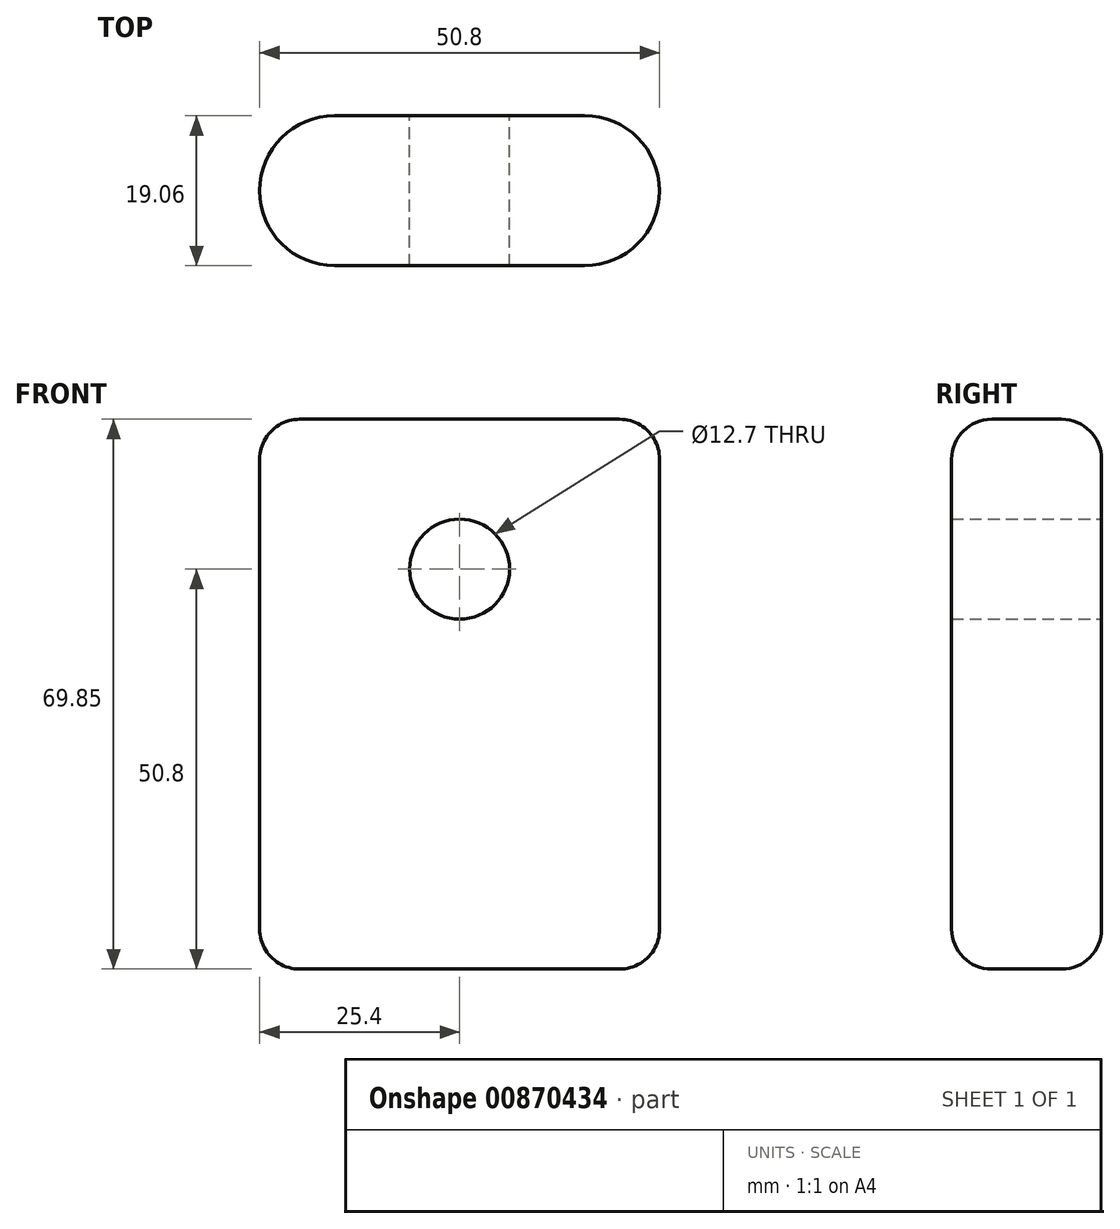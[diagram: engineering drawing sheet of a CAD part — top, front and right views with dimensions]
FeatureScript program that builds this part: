
annotation { "Feature Type Name" : "Feature", "Feature Type Description" : "" }
export const myFeature = defineFeature(function(context is Context, id is Id, definition is map)
    precondition{}
    {
        {
            var Q0;
            Q0=qCreatedBy(makeId("Top.planeOp"),FACE);
            var sketch = newSketch(context, id + "F0", { "sketchPlane" : qUnion([Q0])});
            skLineSegment(sketch, "E0", {"start": v(-15.88, 9.53) * mm, "end": v(15.88, 9.53) * mm});
            skLineSegment(sketch, "E1", {"start": v(-15.88, -9.53) * mm, "end": v(15.88, -9.53) * mm});
            skLineSegment(sketch, "E2", {"start": v(-15.88, 9.53) * mm, "end": v(-15.88, -9.53) * mm, "construction": true});
            skLineSegment(sketch, "E3", {"start": v(15.88, 9.53) * mm, "end": v(15.88, -9.53) * mm, "construction": true});
            skLineSegment(sketch, "E4", {"start": v(-42.6, 0) * mm, "end": v(46.17, 0) * mm, "construction": true});
            skArc(sketch, "E5", {"start": v(-15.88, 9.53) * mm, "mid": v(-25.4, 0) * mm, "end": v(-15.88, -9.53) * mm});
            skArc(sketch, "E6", {"start": v(15.88, 9.52) * mm, "mid": v(25.4, 0) * mm, "end": v(15.88, -9.53) * mm});
            skLineSegment(sketch, "E7", {"start": v(0, 41.34) * mm, "end": v(0, -17.47) * mm, "construction": true});
            skSolve(sketch);
        }
        {
            var Q0;
            Q0=makeQuery(id+"F0.imprint","IMPRINT",FACE,{"disambiguationData":[TD([[makeQuery(id+"F0.imprint","IMPRINT",EDGE,{"derivedFrom":sQuery(id+"F0.wireOp",EDGE,"E0")}),-1.0]])]});
            extrude(context, id + "F1", {"entities" : qUnion([Q0]), "depth" : 69.85 * mm, "offsetDistance" : 25.4 * mm});
        }
        {
            var Q0;
            Q0=makeQuery(id+"F1.opExtrude","CAP_FACE",FACE,{"disambiguationData":[OSD([sQuery(id+"F0.wireOp",EDGE,"E0"),sQuery(id+"F0.wireOp",EDGE,"E1"),sQuery(id+"F0.wireOp",EDGE,"E5"),sQuery(id+"F0.wireOp",EDGE,"E6")])],"isStart":false});
            var Q1;
            Q1=makeQuery(id+"F1.opExtrude","CAP_FACE",FACE,{"disambiguationData":[OSD([sQuery(id+"F0.wireOp",EDGE,"E0"),sQuery(id+"F0.wireOp",EDGE,"E1"),sQuery(id+"F0.wireOp",EDGE,"E5"),sQuery(id+"F0.wireOp",EDGE,"E6")])],"isStart":true});
            fillet(context, id + "F2", {"entities" : qUnion([Q0, Q1]), "radius" : 5.08 * mm, "tangentPropagation" : true, "allowEdgeOverflow" : false});
        }
        {
            var Q0;
            Q0=makeQuery(id+"F1.opExtrude","SWEPT_FACE",FACE,{"disambiguationData":[OSD([sQuery(id+"F0.wireOp",EDGE,"E0")])]});
            var sketch = newSketch(context, id + "F3", { "sketchPlane" : qUnion([Q0])});
            skLineSegment(sketch, "E8", {"start": v(0, -18.72) * mm, "end": v(0, 57.9) * mm, "construction": true});
            skCircle(sketch, "E9", {"center": v(0, 50.8) * mm, "radius": 6.35 * mm});
            skSolve(sketch);
        }
        {
            var Q0;
            Q0=makeQuery(id+"F3.imprint","IMPRINT",FACE,{"disambiguationData":[TD([[makeQuery(id+"F3.imprint","IMPRINT",EDGE,{"derivedFrom":sQuery(id+"F3.wireOp",EDGE,"E9")}),1.0]])]});
            extrude(context, id + "F4", {"entities" : qUnion([Q0]), "operationType" : NewBodyOperationType.REMOVE, "endBound" : BoundingType.THROUGH_ALL, "oppositeDirection" : true, "depth" : 25.4 * mm, "offsetDistance" : 25.4 * mm});
        }
    });
